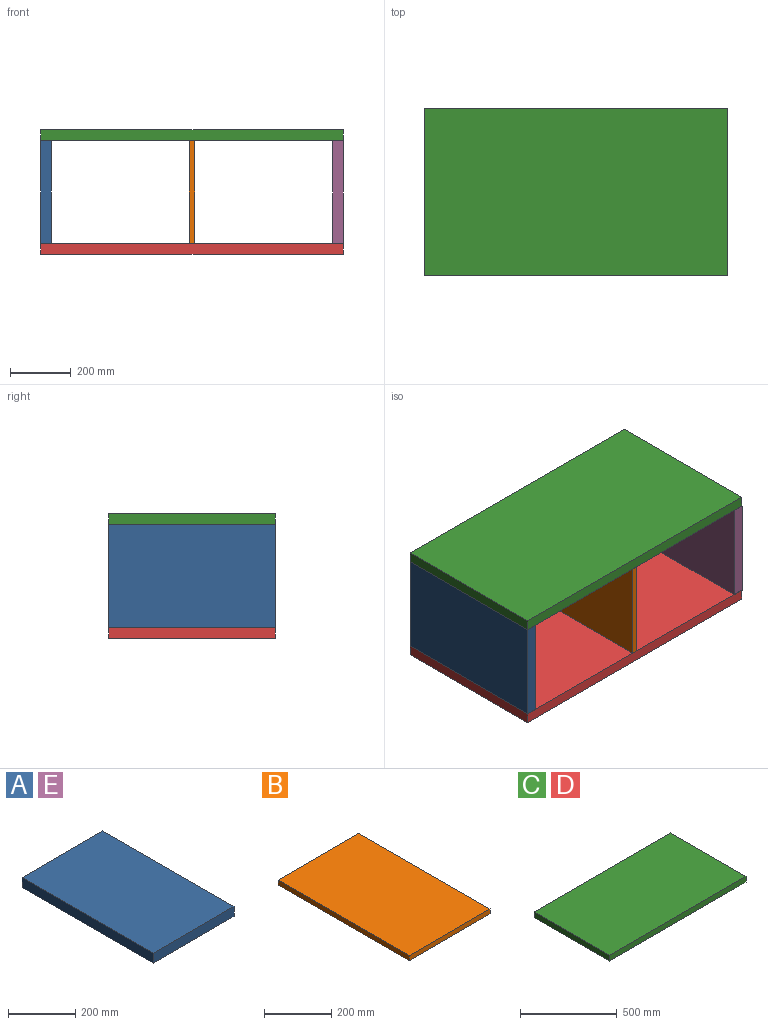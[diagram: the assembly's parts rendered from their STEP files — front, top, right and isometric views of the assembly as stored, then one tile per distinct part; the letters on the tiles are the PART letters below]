
ASSEMBLY  parts=5 mates=4
PART A: 6 faces, bbox 340x550x36 mm
  f0: plane 340x36mm, normal (0,1,0), area 12240mm2, adj f1,f3,f4,f5
  f1: plane 550x36mm, normal (-1,0,0), area 19800mm2, adj f0,f2,f4,f5
  f2: plane 340x36mm, normal (0,-1,0), area 12240mm2, adj f1,f3,f4,f5
  f3: plane 550x36mm, normal (1,0,0), area 19800mm2, adj f0,f2,f4,f5
  f4: plane 550x340mm, normal (0,0,1), area 187000mm2, adj f0,f1,f2,f3
  f5: plane 550x340mm, normal (0,0,-1), area 187000mm2, adj f0,f1,f2,f3
PART B: 6 faces, bbox 340x550x18 mm
  f0: plane 340x18mm, normal (0,1,0), area 6120mm2, adj f1,f3,f4,f5
  f1: plane 550x18mm, normal (-1,0,0), area 9900mm2, adj f0,f2,f4,f5
  f2: plane 340x18mm, normal (0,-1,0), area 6120mm2, adj f1,f3,f4,f5
  f3: plane 550x18mm, normal (1,0,0), area 9900mm2, adj f0,f2,f4,f5
  f4: plane 550x340mm, normal (0,0,1), area 187000mm2, adj f0,f1,f2,f3
  f5: plane 550x340mm, normal (0,0,-1), area 187000mm2, adj f0,f1,f2,f3
PART C: 6 faces, bbox 1000x550x36 mm
  f0: plane 1000x36mm, normal (0,1,0), area 36000mm2, adj f1,f3,f4,f5
  f1: plane 550x36mm, normal (-1,0,0), area 19800mm2, adj f0,f2,f4,f5
  f2: plane 1000x36mm, normal (0,-1,0), area 36000mm2, adj f1,f3,f4,f5
  f3: plane 550x36mm, normal (1,0,0), area 19800mm2, adj f0,f2,f4,f5
  f4: plane 1000x550mm, normal (0,0,1), area 550000mm2, adj f0,f1,f2,f3
  f5: plane 1000x550mm, normal (0,0,-1), area 550000mm2, adj f0,f1,f2,f3
PART D: same geometry as C
PART E: same geometry as A
PLACE A rot(axis=(0,-1,0),90deg) t=(-1329.15,-33.2,-448.12)mm
PLACE B rot(axis=(0,1,0),90deg) t=(-874.15,-33.2,639.48)mm
PLACE C t=(-336.13,-33.2,25.73)mm
PLACE D t=(-336.13,-33.2,-350.27)mm
PLACE E rot(axis=(0,1,0),90deg) t=(-401.15,-33.2,159.58)mm
MATE fastened A.f3 <-> C.f5  axis (0,0,1) through (-1365.15,-4.05,25.73)mm
MATE fastened D.f4 <-> E.f3  axis (0,0,1) through (-365.15,-279.05,-314.27)mm
MATE fastened B.f3 <-> D.f4  axis (0,0,-1) through (-865.15,-279.05,-314.27)mm
MATE fastened E.f1 <-> C.f5  axis (0,0,1) through (-365.15,-279.05,25.73)mm
